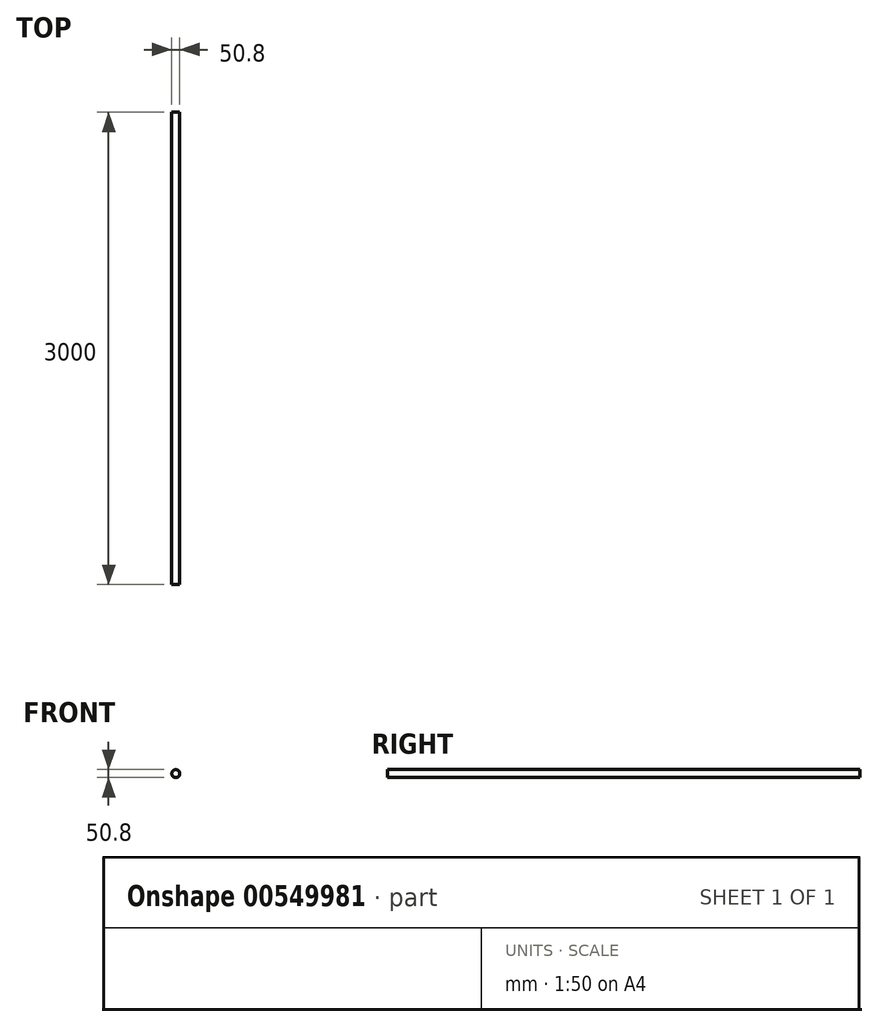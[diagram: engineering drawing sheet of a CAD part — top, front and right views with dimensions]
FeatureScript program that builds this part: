
annotation { "Feature Type Name" : "Feature", "Feature Type Description" : "" }
export const myFeature = defineFeature(function(context is Context, id is Id, definition is map)
    precondition{}
    {
        {
            var Q0;
            Q0=qCreatedBy(makeId("Front.planeOp"),FACE);
            var sketch = newSketch(context, id + "F0", { "sketchPlane" : qUnion([Q0])});
            skCircle(sketch, "E0", {"center": v(0, 0) * mm, "radius": 25.4 * mm});
            skSolve(sketch);
        }
        {
            var Q0;
            Q0 = qSketchRegion(id + "F0", true);
            extrude(context, id + "F1", {"entities" : qUnion([Q0]), "depth" : 3000 * mm, "offsetDistance" : 25.4 * mm});
        }
    });
